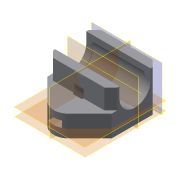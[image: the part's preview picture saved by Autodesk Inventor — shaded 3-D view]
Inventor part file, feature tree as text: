
AUTODESK INVENTOR PART (.ipt)
format: ipt  version: 2015 SP2 (Build 190223200, 223)  size: 206,336 bytes
history: native  units: mm
features: sketch x7, extrude x6, projected_geometry x3, other x2, plane x2, hole x1, revolve x1, mirror x1
ambient origin geometry x8: Origin, YZ Plane, XZ Plane, XY Plane, X Axis, Y Axis, Z Axis, Center Point
bodies: Body1 (feature_tree)
feature tree (23):
  other  "Sólido1"
  extrude  "Extrusión1"  Depth=3.0mm
  extrude  "Extrusión2"  TaperAngle=135.0deg  [1 undecoded]
  extrude  "Extrusión3"  Depth=10.0mm
  hole  "Agujero1"  [1 undecoded]
  plane  "Plano de trabajo1"
  extrude  "Extrusión4"  Depth=22.5mm
  extrude  "Extrusión5"  Depth=12.25mm
  extrude  "Extrusión6"  Depth=10.0mm TaperAngle=0.0deg
  plane  "Plano de trabajo2"
  sketch  "Boceto7"  dims[d21=14.5mm d22=9.25mm d23=0.0mm d57=10.0mm d58=10.0mm d26=3.75mm d27=6.0mm d28=4.0mm d29=2.0mm d30=90.0deg d31=8.0mm d32=20.594885mm d35=4.0mm d36=6.235mm d37=6.0mm d38=3.0mm d39=0.0mm d44=27.0mm d45=23.0mm d46=2.0mm d47=4.5mm d48=0.0mm d49=15.2mm d50=24.2mm d51=0.0mm d52=0.116mm d53=1.23mm d54=90.0deg d55=27.25mm d59=7.0mm d60=34.25mm]
  other  "Eje de trabajo1"
  revolve  "Revolución1"  [1 undecoded]
  mirror  "Simetría1"
  sketch  "Boceto1"  dims[d0=30.0mm d5=3.0mm]
  sketch  "Boceto2"  dims[d6=3.0mm d10=135.0deg]
  projected_geometry  "Contorno proyectado1"
  sketch  "Boceto3"  dims[d11=10.0mm d12=0.0mm d13=3.0mm]
  sketch  "Boceto4"  dims[d14=3.0mm d15=3.0mm]
  sketch  "Boceto5"  dims[d16=3.0mm d17=22.5mm]
  sketch  "Boceto6"  dims[d18=9.25mm d19=0.0mm d20=12.25mm]
  projected_geometry  "Contorno proyectado2"
  projected_geometry  "Contorno proyectado3"
note: 3 required parameter values undecoded (feature->parameter linkage not recoverable at this tier; creation-order binding heuristic only, values carry confidence <= 0.55)